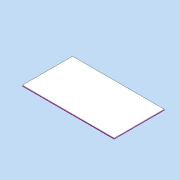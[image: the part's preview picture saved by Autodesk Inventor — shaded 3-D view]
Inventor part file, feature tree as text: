
AUTODESK INVENTOR PART (.ipt)
format: ipt  version: unknown  size: 4,499,968 bytes
history: native  units: mm
features: sketch x7, other x6, extrude x1
ambient origin geometry x8: Origin, YZ Plane, XZ Plane, XY Plane, X Axis, Y Axis, Z Axis, Center Point
feature tree (14):
  sketch  "Эскиз1"
  extrude  "Выдавливание1"  Depth=55.0mm
  other  "Рельеф2"
  other  "Рельеф3"
  sketch  "Эскиз10"
  other  "Рельеф4"
  other  "Рельеф6"
  other  "Рельеф7"
  other  "Рельеф10"
  sketch  "Эскиз8"
  sketch  "Эскиз9"
  sketch  "Эскиз11"
  sketch  "Эскиз13"
  sketch  "Эскиз16"
